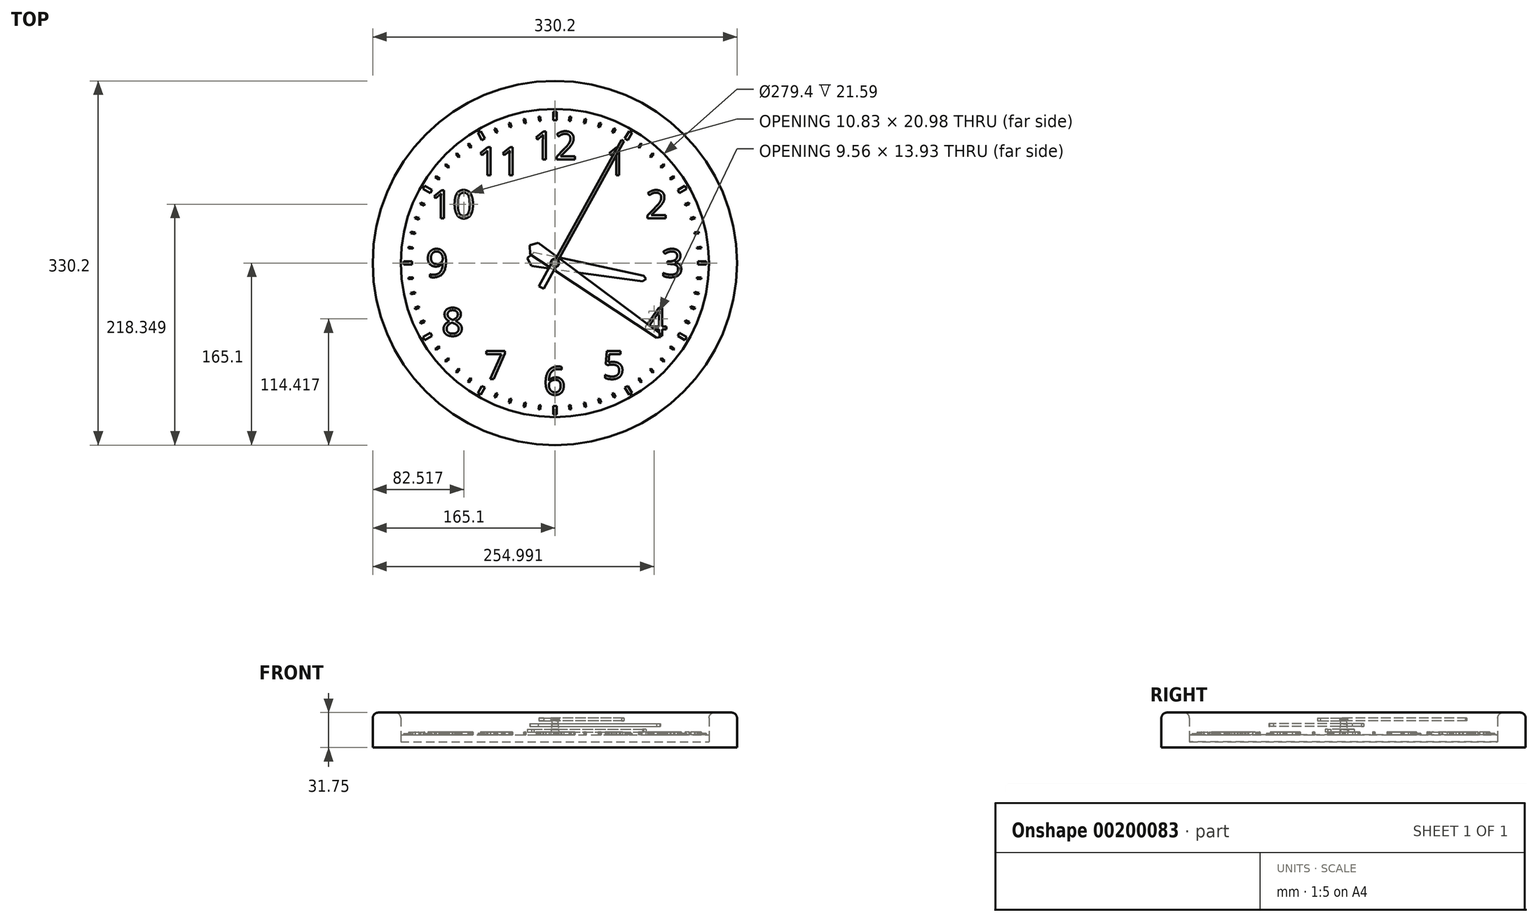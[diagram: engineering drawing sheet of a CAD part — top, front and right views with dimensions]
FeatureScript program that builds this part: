
annotation { "Feature Type Name" : "Feature", "Feature Type Description" : "" }
export const myFeature = defineFeature(function(context is Context, id is Id, definition is map)
    precondition{}
    {
        {
            var Q0;
            Q0=qCreatedBy(makeId("Front.planeOp"),FACE);
            var sketch = newSketch(context, id + "F0", { "sketchPlane" : qUnion([Q0])});
            skLineSegment(sketch, "E0", {"start": v(0, 0) * mm, "end": v(0, 54.8) * mm, "construction": true});
            skLineSegment(sketch, "E1.bottom", {"start": v(139.7, 0) * mm, "end": v(165.1, 0) * mm});
            skLineSegment(sketch, "E1.top", {"start": v(139.7, 31.75) * mm, "end": v(165.1, 31.75) * mm});
            skLineSegment(sketch, "E1.left", {"start": v(139.7, 5.08) * mm, "end": v(139.7, 31.75) * mm});
            skLineSegment(sketch, "E1.right", {"start": v(165.1, 0) * mm, "end": v(165.1, 31.75) * mm});
            skLineSegment(sketch, "E2", {"start": v(152.4, 0) * mm, "end": v(152.4, 31.75) * mm, "construction": true});
            skLineSegment(sketch, "E3.bottom", {"start": v(0, 0) * mm, "end": v(139.7, 0) * mm});
            skLineSegment(sketch, "E3.top", {"start": v(0, 5.08) * mm, "end": v(139.7, 5.08) * mm});
            skLineSegment(sketch, "E3.left", {"start": v(0, 0) * mm, "end": v(0, 5.08) * mm});
            skSolve(sketch);
        }
        {
            var Q0;
            Q0=makeQuery(id+"F0.imprint","IMPRINT",FACE,{"disambiguationData":[TD([[makeQuery(id+"F0.imprint","IMPRINT",EDGE,{"derivedFrom":sQuery(id+"F0.wireOp",EDGE,"E1.bottom")}),1.0]])]});
            var Q1;
            Q1=sQuery(id+"F0.wireOp",EDGE,"E0");
            revolve(context, id + "F1", {"entities" : qUnion([Q0]), "axis" : qUnion([Q1]), "revolveType" : RevolveType.FULL});
        }
        {
            var Q0;
            Q0=makeQuery(id+"F1.opRevolve","SWEPT_EDGE",EDGE,{"disambiguationData":[OSD([sQuery(id+"F0.wireOp",EDGE,"E1.top"),sQuery(id+"F0.wireOp",EDGE,"E1.left")])]});
            var Q1;
            Q1=makeQuery(id+"F1.opRevolve","SWEPT_EDGE",EDGE,{"disambiguationData":[OSD([sQuery(id+"F0.wireOp",EDGE,"E1.top"),sQuery(id+"F0.wireOp",EDGE,"E1.right")])]});
            fillet(context, id + "F2", {"entities" : qUnion([Q0, Q1]), "radius" : 5.08 * mm, "tangentPropagation" : true, "allowEdgeOverflow" : false});
        }
        {
            var Q0;
            Q0=makeQuery(id+"F1.opRevolve","SWEPT_FACE",FACE,{"disambiguationData":[OSD([sQuery(id+"F0.wireOp",EDGE,"E3.top")])]});
            extrude(context, id + "F3", {"entities" : qUnion([Q0]), "depth" : 6.35 * mm});
        }
        {
            var Q0;
            Q0=makeQuery(id+"F3.opExtrude","CAP_FACE",FACE,{"disambiguationData":[OSD([sQuery(id+"F0.wireOp",EDGE,"E3.top")])],"isStart":false});
            var sketch = newSketch(context, id + "F4", { "sketchPlane" : qUnion([Q0])});
            skText(sketch, "E4", { "text": "12", "fontName": "OpenSans-Regular.ttf"});
            skLineSegment(sketch, "E5", {"start": v(0, 0) * mm, "end": v(0, 106.68) * mm, "construction": true});
            skLineSegment(sketch, "E6.1.0", {"start": v(0, 0) * mm, "end": v(-53.34, 92.39) * mm, "construction": true});
            skLineSegment(sketch, "E6.2.0", {"start": v(0, 0) * mm, "end": v(-92.39, 53.34) * mm, "construction": true});
            skLineSegment(sketch, "E6.3.0", {"start": v(0, 0) * mm, "end": v(-106.68, 0) * mm, "construction": true});
            skLineSegment(sketch, "E6.4.0", {"start": v(0, 0) * mm, "end": v(-92.39, -53.34) * mm, "construction": true});
            skLineSegment(sketch, "E6.5.0", {"start": v(0, 0) * mm, "end": v(-53.34, -92.39) * mm, "construction": true});
            skLineSegment(sketch, "E6.6.0", {"start": v(0, 0) * mm, "end": v(0, -106.68) * mm, "construction": true});
            skLineSegment(sketch, "E6.7.0", {"start": v(0, 0) * mm, "end": v(53.34, -92.39) * mm, "construction": true});
            skLineSegment(sketch, "E6.8.0", {"start": v(0, 0) * mm, "end": v(92.39, -53.34) * mm, "construction": true});
            skLineSegment(sketch, "E6.9.0", {"start": v(0, 0) * mm, "end": v(106.68, 0) * mm, "construction": true});
            skLineSegment(sketch, "E6.10.0", {"start": v(0, 0) * mm, "end": v(92.39, 53.34) * mm, "construction": true});
            skLineSegment(sketch, "E6.11.0", {"start": v(0, 0) * mm, "end": v(53.34, 92.39) * mm, "construction": true});
            skPoint(sketch, "E6.center", {"position": v(0, 0) * mm});
            skText(sketch, "E7", { "text": "2", "fontName": "OpenSans-Regular.ttf"});
            skText(sketch, "E8", { "text": "3", "fontName": "OpenSans-Regular.ttf"});
            skText(sketch, "E9", { "text": "4", "fontName": "OpenSans-Regular.ttf"});
            skText(sketch, "E10", { "text": "1", "fontName": "OpenSans-Regular.ttf"});
            skText(sketch, "E11", { "text": "5", "fontName": "OpenSans-Regular.ttf"});
            skText(sketch, "E12", { "text": "6", "fontName": "OpenSans-Regular.ttf"});
            skText(sketch, "E13", { "text": "7", "fontName": "OpenSans-Regular.ttf"});
            skText(sketch, "E14", { "text": "9", "fontName": "OpenSans-Regular.ttf"});
            skText(sketch, "E15", { "text": "8", "fontName": "OpenSans-Regular.ttf"});
            skText(sketch, "E16", { "text": "10", "fontName": "OpenSans-Regular.ttf"});
            skText(sketch, "E17", { "text": "11", "fontName": "OpenSans-Regular.ttf"});
            const initialGuessF4  = {"E4": [-0.02037, 0.09398, 1, 0, 0.0254], "E7": [0.0821, 0.04064, 1, 0, 0.0254], "E8": [0.09649, -0.0127, 1, 0, 0.0254], "E9": [0.08151, -0.06604, 1, 0, 0.0254], "E10": [0.04604, 0.07969, 1, 0, 0.0254], "E11": [0.04313, -0.10509, 1, 0, 0.0254], "E12": [-0.01037, -0.11938, 1, 0, 0.0254], "E13": [-0.06367, -0.10509, 1, 0, 0.0254], "E14": [-0.11696, -0.0127, 1, 0, 0.0254], "E15": [-0.1027, -0.06604, 1, 0, 0.0254], "E16": [-0.11282, 0.04064, 1, 0, 0.0254], "E17": [-0.07073, 0.07969, 1, 0, 0.0254]};
            skSetInitialGuess(sketch, initialGuessF4);
            skSolve(sketch);
        }
        {
            var Q0;
            Q0=qSketchRegion(id+"F4",true);
            extrude(context, id + "F5", {"entities" : qUnion([Q0]), "depth" : 2.54 * mm});
        }
        {
            var Q0;
            Q0=makeQuery(id+"F3.opExtrude","CAP_FACE",FACE,{"disambiguationData":[OSD([sQuery(id+"F0.wireOp",EDGE,"E3.top")])],"isStart":false});
            var sketch = newSketch(context, id + "F6", { "sketchPlane" : qUnion([Q0])});
            skCircle(sketch, "E18", {"center": v(0, 0) * mm, "radius": 3.81 * mm});
            skSolve(sketch);
        }
        {
            var Q0;
            Q0=makeQuery(id+"F6.imprint","IMPRINT",FACE,{"disambiguationData":[TD([[makeQuery(id+"F6.imprint","IMPRINT",EDGE,{"derivedFrom":sQuery(id+"F6.wireOp",EDGE,"E18")}),-1.0]])]});
            cPlane(context, id + "F7", {"entities" : qUnion([Q0]), "cplaneType" : CPlaneType.OFFSET, "offset" : 13.97 * mm, "width" : 152.4 * mm, "height" : 152.4 * mm});
        }
        {
            var Q0;
            Q0=qCreatedBy(id+"F7.planeOp",FACE);
            var sketch = newSketch(context, id + "F8", { "sketchPlane" : qUnion([Q0])});
            skCircle(sketch, "E19", {"center": v(0, 0) * mm, "radius": 2.54 * mm});
            skSolve(sketch);
        }
        {
            var Q1;
            Q1=makeQuery(id+"F6.imprint","IMPRINT",FACE,{"disambiguationData":[TD([[makeQuery(id+"F6.imprint","IMPRINT",EDGE,{"derivedFrom":sQuery(id+"F6.wireOp",EDGE,"E18")}),1.0]])]});
            var Q2;
            Q2=makeQuery(id+"F8.imprint","IMPRINT",FACE,{"disambiguationData":[TD([[makeQuery(id+"F8.imprint","IMPRINT",EDGE,{"derivedFrom":sQuery(id+"F8.wireOp",EDGE,"E19")}),1.0]])]});
            loft(context, id + "F9", {"sheetProfilesArray" : [{ "sheetProfileEntities" : qUnion([Q1]) }, { "sheetProfileEntities" : qUnion([Q2]) }]});
        }
        {
            var Q0;
            Q0=makeQuery(id+"F3.opExtrude","CAP_FACE",FACE,{"disambiguationData":[OSD([sQuery(id+"F0.wireOp",EDGE,"E3.top")])],"isStart":false});
            cPlane(context, id + "F10", {"entities" : qUnion([Q0]), "cplaneType" : CPlaneType.OFFSET, "offset" : 2.54 * mm, "width" : 152.4 * mm, "height" : 152.4 * mm});
        }
        {
            var Q0;
            Q0=qCreatedBy(id+"F10.planeOp",FACE);
            var sketch = newSketch(context, id + "F11", { "sketchPlane" : qUnion([Q0])});
            skLineSegment(sketch, "E20", {"start": v(5, -0.88) * mm, "end": v(80.05, -14.11) * mm, "construction": true});
            skLineSegment(sketch, "E21", {"start": v(80.05, -14.11) * mm, "end": v(79.6, -16.62) * mm, "construction": true});
            skLineSegment(sketch, "E22", {"start": v(-20.01, 3.53) * mm, "end": v(-21.11, -2.72) * mm, "construction": true});
            skLineSegment(sketch, "E23", {"start": v(5, -0.88) * mm, "end": v(-25.01, 4.41) * mm, "construction": true});
            skLineSegment(sketch, "E24", {"start": v(-25.01, 4.41) * mm, "end": v(-21.11, -2.72) * mm});
            skLineSegment(sketch, "E25", {"start": v(-21.11, -2.72) * mm, "end": v(79.6, -16.62) * mm});
            skLineSegment(sketch, "E26", {"start": v(80.05, -14.11) * mm, "end": v(82.55, -14.56) * mm, "construction": true});
            skLineSegment(sketch, "E27", {"start": v(82.55, -14.56) * mm, "end": v(79.6, -16.62) * mm});
            skLineSegment(sketch, "E28.MirrorCS", {"start": v(82.55, -14.56) * mm, "end": v(80.49, -11.61) * mm});
            skLineSegment(sketch, "E29.MirrorCS", {"start": v(-18.9, 9.78) * mm, "end": v(80.49, -11.61) * mm});
            skLineSegment(sketch, "E30.MirrorCS", {"start": v(-25.01, 4.41) * mm, "end": v(-18.9, 9.78) * mm});
            skSolve(sketch);
        }
        {
            var Q0;
            Q0=makeQuery(id+"F11.imprint","IMPRINT",FACE,{"disambiguationData":[TD([[makeQuery(id+"F11.imprint","IMPRINT",EDGE,{"derivedFrom":sQuery(id+"F11.wireOp",EDGE,"E24")}),1.0]])]});
            var Q1;
            Q1=makeQuery(id+"F11.imprint","IMPRINT",FACE,{"disambiguationData":[TD([[makeQuery(id+"F11.imprint","IMPRINT",EDGE,{"derivedFrom":makeQuery(id+"F9.opLoft","MID_CAP_EDGE",EDGE,{"disambiguationData":[OSD([sQuery(id+"F6.wireOp",EDGE,"E18")])],"capPos":0.0})}),1.0]])]});
            extrude(context, id + "F12", {"entities" : qUnion([Q0, Q1]), "depth" : 2.54 * mm});
        }
        {
            var Q0;
            Q0=makeQuery(id+"F12.opExtrude","CAP_FACE",FACE,{"disambiguationData":[OSD([sQuery(id+"F11.wireOp",EDGE,"E24"),sQuery(id+"F11.wireOp",EDGE,"E25"),sQuery(id+"F11.wireOp",EDGE,"E27"),sQuery(id+"F11.wireOp",EDGE,"E28.MirrorCS"),sQuery(id+"F11.wireOp",EDGE,"E29.MirrorCS"),sQuery(id+"F11.wireOp",EDGE,"E30.MirrorCS")])],"isStart":false});
            cPlane(context, id + "F13", {"entities" : qUnion([Q0]), "cplaneType" : CPlaneType.OFFSET, "offset" : 2.54 * mm, "width" : 152.4 * mm, "height" : 152.4 * mm});
        }
        {
            var Q0;
            Q0=qCreatedBy(id+"F13.planeOp",FACE);
            var sketch = newSketch(context, id + "F14", { "sketchPlane" : qUnion([Q0])});
            skLineSegment(sketch, "E31", {"start": v(0, 0) * mm, "end": v(95.7, -67.02) * mm, "construction": true});
            skLineSegment(sketch, "E32", {"start": v(0, 0) * mm, "end": v(-22.89, 16.03) * mm, "construction": true});
            skLineSegment(sketch, "E33", {"start": v(-18.73, 13.11) * mm, "end": v(-15.08, 18.31) * mm, "construction": true});
            skLineSegment(sketch, "E34", {"start": v(93.63, -65.56) * mm, "end": v(95.09, -63.48) * mm, "construction": true});
            skLineSegment(sketch, "E35", {"start": v(-22.89, 16.03) * mm, "end": v(-15.08, 18.31) * mm});
            skLineSegment(sketch, "E36", {"start": v(-15.08, 18.31) * mm, "end": v(95.09, -63.48) * mm});
            skLineSegment(sketch, "E37", {"start": v(95.09, -63.48) * mm, "end": v(95.7, -67.02) * mm});
            skLineSegment(sketch, "E38.MirrorCS", {"start": v(-22.89, 16.03) * mm, "end": v(-22.37, 7.91) * mm});
            skLineSegment(sketch, "E39.MirrorCS", {"start": v(-22.37, 7.91) * mm, "end": v(92.17, -67.64) * mm});
            skLineSegment(sketch, "E40.MirrorCS", {"start": v(92.17, -67.64) * mm, "end": v(95.7, -67.02) * mm});
            skLineSegment(sketch, "E41", {"start": v(0, 0) * mm, "end": v(0, -35.35) * mm, "construction": true});
            skSolve(sketch);
        }
        {
            var Q0;
            Q0=makeQuery(id+"F14.imprint","IMPRINT",FACE,{"disambiguationData":[TD([[makeQuery(id+"F14.imprint","IMPRINT",EDGE,{"derivedFrom":sQuery(id+"F14.wireOp",EDGE,"E35")}),-1.0]])]});
            extrude(context, id + "F15", {"entities" : qUnion([Q0]), "depth" : 2.54 * mm});
        }
        {
            var Q0;
            Q0=makeQuery(id+"F15.opExtrude","CAP_FACE",FACE,{"disambiguationData":[OSD([sQuery(id+"F14.wireOp",EDGE,"E35"),sQuery(id+"F14.wireOp",EDGE,"E36"),sQuery(id+"F14.wireOp",EDGE,"E37"),sQuery(id+"F14.wireOp",EDGE,"E38.MirrorCS"),sQuery(id+"F14.wireOp",EDGE,"E39.MirrorCS"),sQuery(id+"F14.wireOp",EDGE,"E40.MirrorCS")])],"isStart":false});
            cPlane(context, id + "F16", {"entities" : qUnion([Q0]), "cplaneType" : CPlaneType.OFFSET, "offset" : 2.54 * mm, "width" : 152.4 * mm, "height" : 152.4 * mm});
        }
        {
            var Q0;
            Q0=qCreatedBy(id+"F16.planeOp",FACE);
            var sketch = newSketch(context, id + "F17", { "sketchPlane" : qUnion([Q0])});
            skArc(sketch, "E42", {"start": v(0.85, -3.72) * mm, "mid": v(3.63, -1.17) * mm, "end": v(2.85, 2.53) * mm});
            skLineSegment(sketch, "E43", {"start": v(0, 0) * mm, "end": v(61.55, 111.09) * mm, "construction": true});
            skLineSegment(sketch, "E44", {"start": v(0, 0) * mm, "end": v(-12.31, -22.22) * mm, "construction": true});
            skLineSegment(sketch, "E45", {"start": v(-12.31, -22.22) * mm, "end": v(-10.09, -23.45) * mm});
            skLineSegment(sketch, "E46", {"start": v(-10.09, -23.45) * mm, "end": v(0.85, -3.72) * mm});
            skLineSegment(sketch, "E47", {"start": v(61.55, 111.09) * mm, "end": v(62.66, 110.47) * mm});
            skLineSegment(sketch, "E48", {"start": v(62.66, 110.47) * mm, "end": v(2.85, 2.53) * mm});
            skLineSegment(sketch, "E49.MirrorCS", {"start": v(61.55, 111.09) * mm, "end": v(60.44, 111.7) * mm});
            skLineSegment(sketch, "E50.MirrorCS", {"start": v(60.44, 111.7) * mm, "end": v(0.63, 3.76) * mm});
            skArc(sketch, "E51.MirrorCS", {"start": v(-3.6, -1.25) * mm, "mid": v(-2.91, 2.46) * mm, "end": v(0.63, 3.76) * mm});
            skLineSegment(sketch, "E52.MirrorCS", {"start": v(-14.53, -20.99) * mm, "end": v(-3.6, -1.25) * mm});
            skLineSegment(sketch, "E53.MirrorCS", {"start": v(-12.31, -22.22) * mm, "end": v(-14.53, -20.99) * mm});
            skSolve(sketch);
        }
        {
            var Q0;
            Q0=makeQuery(id+"F17.imprint","IMPRINT",FACE,{"disambiguationData":[TD([[makeQuery(id+"F17.imprint","IMPRINT",EDGE,{"derivedFrom":sQuery(id+"F17.wireOp",EDGE,"E42")}),1.0]])]});
            extrude(context, id + "F18", {"entities" : qUnion([Q0]), "depth" : 2.54 * mm});
        }
        {
            var Q0;
            Q0=makeQuery(id+"F9.opLoft","SWEPT_BODY",BODY,{"disambiguationData":[OSD([makeQuery(id+"F6.imprint","IMPRINT",FACE,{"disambiguationData":[TD([[makeQuery(id+"F6.imprint","IMPRINT",EDGE,{"derivedFrom":sQuery(id+"F6.wireOp",EDGE,"E18")}),1.0]])]}),makeQuery(id+"F8.imprint","IMPRINT",FACE,{"disambiguationData":[TD([[makeQuery(id+"F8.imprint","IMPRINT",EDGE,{"derivedFrom":sQuery(id+"F8.wireOp",EDGE,"E19")}),1.0]])]})])]});
            var Q1;
            Q1=makeQuery(id+"F12.opExtrude","SWEPT_BODY",BODY,{"disambiguationData":[OSD([sQuery(id+"F11.wireOp",EDGE,"E24"),sQuery(id+"F11.wireOp",EDGE,"E25"),sQuery(id+"F11.wireOp",EDGE,"E27"),sQuery(id+"F11.wireOp",EDGE,"E28.MirrorCS"),sQuery(id+"F11.wireOp",EDGE,"E29.MirrorCS"),sQuery(id+"F11.wireOp",EDGE,"E30.MirrorCS")])]});
            booleanBodies(context, id + "F19", {"operationType" : BooleanOperationType.SUBTRACTION, "tools" : qUnion([Q0]), "targets" : qUnion([Q1]), "keepTools" : true});
        }
        {
            var Q0;
            Q0=makeQuery(id+"F9.opLoft","SWEPT_BODY",BODY,{"disambiguationData":[OSD([makeQuery(id+"F6.imprint","IMPRINT",FACE,{"disambiguationData":[TD([[makeQuery(id+"F6.imprint","IMPRINT",EDGE,{"derivedFrom":sQuery(id+"F6.wireOp",EDGE,"E18")}),1.0]])]}),makeQuery(id+"F8.imprint","IMPRINT",FACE,{"disambiguationData":[TD([[makeQuery(id+"F8.imprint","IMPRINT",EDGE,{"derivedFrom":sQuery(id+"F8.wireOp",EDGE,"E19")}),1.0]])]})])]});
            var Q1;
            Q1=makeQuery(id+"F15.opExtrude","SWEPT_BODY",BODY,{"disambiguationData":[OSD([sQuery(id+"F14.wireOp",EDGE,"E35"),sQuery(id+"F14.wireOp",EDGE,"E36"),sQuery(id+"F14.wireOp",EDGE,"E37"),sQuery(id+"F14.wireOp",EDGE,"E38.MirrorCS"),sQuery(id+"F14.wireOp",EDGE,"E39.MirrorCS"),sQuery(id+"F14.wireOp",EDGE,"E40.MirrorCS")])]});
            booleanBodies(context, id + "F20", {"operationType" : BooleanOperationType.SUBTRACTION, "tools" : qUnion([Q0]), "targets" : qUnion([Q1]), "keepTools" : true});
        }
        {
            var Q0;
            Q0=makeQuery(id+"F9.opLoft","SWEPT_BODY",BODY,{"disambiguationData":[OSD([makeQuery(id+"F6.imprint","IMPRINT",FACE,{"disambiguationData":[TD([[makeQuery(id+"F6.imprint","IMPRINT",EDGE,{"derivedFrom":sQuery(id+"F6.wireOp",EDGE,"E18")}),1.0]])]}),makeQuery(id+"F8.imprint","IMPRINT",FACE,{"disambiguationData":[TD([[makeQuery(id+"F8.imprint","IMPRINT",EDGE,{"derivedFrom":sQuery(id+"F8.wireOp",EDGE,"E19")}),1.0]])]})])]});
            var Q1;
            Q1=makeQuery(id+"F18.opExtrude","SWEPT_BODY",BODY,{"disambiguationData":[OSD([sQuery(id+"F17.wireOp",EDGE,"E42"),sQuery(id+"F17.wireOp",EDGE,"E45"),sQuery(id+"F17.wireOp",EDGE,"E46"),sQuery(id+"F17.wireOp",EDGE,"E47"),sQuery(id+"F17.wireOp",EDGE,"E48"),sQuery(id+"F17.wireOp",EDGE,"E49.MirrorCS"),sQuery(id+"F17.wireOp",EDGE,"E50.MirrorCS"),sQuery(id+"F17.wireOp",EDGE,"E51.MirrorCS"),sQuery(id+"F17.wireOp",EDGE,"E52.MirrorCS"),sQuery(id+"F17.wireOp",EDGE,"E53.MirrorCS")])]});
            booleanBodies(context, id + "F21", {"operationType" : BooleanOperationType.SUBTRACTION, "tools" : qUnion([Q0]), "targets" : qUnion([Q1]), "keepTools" : true});
        }
        {
            var Q0;
            Q0=makeQuery(id+"F19.opBoolean","INTERSECT",EDGE,{"derivedFrom":[makeQuery(id+"F9.opLoft","SWEPT_FACE",FACE,{"disambiguationData":[OSD([sQuery(id+"F6.wireOp",EDGE,"E18"),sQuery(id+"F8.wireOp",EDGE,"E19")])]}),makeQuery(id+"F12.opExtrude","CAP_FACE",FACE,{"disambiguationData":[OSD([sQuery(id+"F11.wireOp",EDGE,"E24"),sQuery(id+"F11.wireOp",EDGE,"E25"),sQuery(id+"F11.wireOp",EDGE,"E27"),sQuery(id+"F11.wireOp",EDGE,"E28.MirrorCS"),sQuery(id+"F11.wireOp",EDGE,"E29.MirrorCS"),sQuery(id+"F11.wireOp",EDGE,"E30.MirrorCS")])],"isStart":true})]});
            var Q1;
            Q1=makeQuery(id+"F19.opBoolean","INTERSECT",EDGE,{"derivedFrom":[makeQuery(id+"F9.opLoft","SWEPT_FACE",FACE,{"disambiguationData":[OSD([sQuery(id+"F6.wireOp",EDGE,"E18"),sQuery(id+"F8.wireOp",EDGE,"E19")])]}),makeQuery(id+"F12.opExtrude","CAP_FACE",FACE,{"disambiguationData":[OSD([sQuery(id+"F11.wireOp",EDGE,"E24"),sQuery(id+"F11.wireOp",EDGE,"E25"),sQuery(id+"F11.wireOp",EDGE,"E27"),sQuery(id+"F11.wireOp",EDGE,"E28.MirrorCS"),sQuery(id+"F11.wireOp",EDGE,"E29.MirrorCS"),sQuery(id+"F11.wireOp",EDGE,"E30.MirrorCS")])],"isStart":false})]});
            var Q2;
            Q2=makeQuery(id+"F20.opBoolean","INTERSECT",EDGE,{"derivedFrom":[makeQuery(id+"F9.opLoft","SWEPT_FACE",FACE,{"disambiguationData":[OSD([sQuery(id+"F6.wireOp",EDGE,"E18"),sQuery(id+"F8.wireOp",EDGE,"E19")])]}),makeQuery(id+"F15.opExtrude","CAP_FACE",FACE,{"disambiguationData":[OSD([sQuery(id+"F14.wireOp",EDGE,"E35"),sQuery(id+"F14.wireOp",EDGE,"E36"),sQuery(id+"F14.wireOp",EDGE,"E37"),sQuery(id+"F14.wireOp",EDGE,"E38.MirrorCS"),sQuery(id+"F14.wireOp",EDGE,"E39.MirrorCS"),sQuery(id+"F14.wireOp",EDGE,"E40.MirrorCS")])],"isStart":true})]});
            var Q3;
            Q3=makeQuery(id+"F20.opBoolean","INTERSECT",EDGE,{"derivedFrom":[makeQuery(id+"F9.opLoft","SWEPT_FACE",FACE,{"disambiguationData":[OSD([sQuery(id+"F6.wireOp",EDGE,"E18"),sQuery(id+"F8.wireOp",EDGE,"E19")])]}),makeQuery(id+"F15.opExtrude","CAP_FACE",FACE,{"disambiguationData":[OSD([sQuery(id+"F14.wireOp",EDGE,"E35"),sQuery(id+"F14.wireOp",EDGE,"E36"),sQuery(id+"F14.wireOp",EDGE,"E37"),sQuery(id+"F14.wireOp",EDGE,"E38.MirrorCS"),sQuery(id+"F14.wireOp",EDGE,"E39.MirrorCS"),sQuery(id+"F14.wireOp",EDGE,"E40.MirrorCS")])],"isStart":false})]});
            var Q4;
            Q4=makeQuery(id+"F21.opBoolean","INTERSECT",EDGE,{"derivedFrom":[makeQuery(id+"F9.opLoft","SWEPT_FACE",FACE,{"disambiguationData":[OSD([sQuery(id+"F6.wireOp",EDGE,"E18"),sQuery(id+"F8.wireOp",EDGE,"E19")])]}),makeQuery(id+"F18.opExtrude","CAP_FACE",FACE,{"disambiguationData":[OSD([sQuery(id+"F17.wireOp",EDGE,"E42"),sQuery(id+"F17.wireOp",EDGE,"E45"),sQuery(id+"F17.wireOp",EDGE,"E46"),sQuery(id+"F17.wireOp",EDGE,"E47"),sQuery(id+"F17.wireOp",EDGE,"E48"),sQuery(id+"F17.wireOp",EDGE,"E49.MirrorCS"),sQuery(id+"F17.wireOp",EDGE,"E50.MirrorCS"),sQuery(id+"F17.wireOp",EDGE,"E51.MirrorCS"),sQuery(id+"F17.wireOp",EDGE,"E52.MirrorCS"),sQuery(id+"F17.wireOp",EDGE,"E53.MirrorCS")])],"isStart":true})]});
            var Q5;
            Q5=makeQuery(id+"F21.opBoolean","COPY",EDGE,{"derivedFrom":makeQuery(id+"F9.opLoft","MID_CAP_EDGE",EDGE,{"disambiguationData":[OSD([sQuery(id+"F6.wireOp",EDGE,"E18"),sQuery(id+"F8.wireOp",EDGE,"E19")])],"capPos":1.0})});
            chamfer(context, id + "F22", {"entities" : qUnion([Q0, Q1, Q2, Q3, Q4, Q5]), "width" : 0.25 * mm, "tangentPropagation" : true});
        }
        {
            var Q0;
            Q0=makeQuery(id+"F3.opExtrude","CAP_FACE",FACE,{"disambiguationData":[OSD([sQuery(id+"F0.wireOp",EDGE,"E3.top")])],"isStart":false});
            var sketch = newSketch(context, id + "F23", { "sketchPlane" : qUnion([Q0])});
            skLineSegment(sketch, "E54", {"start": v(0, 0) * mm, "end": v(0, 139.7) * mm, "construction": true});
            skLineSegment(sketch, "E55.bottom", {"start": v(1.52, 137.16) * mm, "end": v(-1.52, 137.16) * mm});
            skLineSegment(sketch, "E55.top", {"start": v(1.52, 129.54) * mm, "end": v(-1.52, 129.54) * mm});
            skLineSegment(sketch, "E55.left", {"start": v(1.52, 137.16) * mm, "end": v(1.52, 129.54) * mm});
            skLineSegment(sketch, "E55.right", {"start": v(-1.52, 137.16) * mm, "end": v(-1.52, 129.54) * mm});
            skPoint(sketch, "E55.middle", {"position": v(0, 133.35) * mm});
            skSolve(sketch);
        }
        {
            var Q0;
            Q0=makeQuery(id+"F23.imprint","IMPRINT",FACE,{"disambiguationData":[TD([[makeQuery(id+"F23.imprint","IMPRINT",EDGE,{"derivedFrom":sQuery(id+"F23.wireOp",EDGE,"E55.bottom")}),1.0]])]});
            extrude(context, id + "F24", {"entities" : qUnion([Q0]), "depth" : 1.27 * mm});
        }
        {
            var Q0;
            Q0=makeQuery(id+"F24.opExtrude","SWEPT_BODY",BODY,{"disambiguationData":[OSD([sQuery(id+"F23.wireOp",EDGE,"E55.bottom"),sQuery(id+"F23.wireOp",EDGE,"E55.top"),sQuery(id+"F23.wireOp",EDGE,"E55.left"),sQuery(id+"F23.wireOp",EDGE,"E55.right")])]});
            var Q1;
            Q1=sQuery(id+"F0.wireOp",EDGE,"E0");
            circularPattern(context, id + "F25", {"entities" : qUnion([Q0]), "axis" : qUnion([Q1]), "angle" : 360 * degree, "instanceCount" : 12, "equalSpace" : true});
        }
        {
            var Q0;
            Q0=makeQuery(id+"F3.opExtrude","CAP_FACE",FACE,{"disambiguationData":[OSD([sQuery(id+"F0.wireOp",EDGE,"E3.top")])],"isStart":false});
            var sketch = newSketch(context, id + "F26", { "sketchPlane" : qUnion([Q0])});
            skLineSegment(sketch, "E56", {"start": v(0, 0) * mm, "end": v(0, 65.46) * mm, "construction": true});
            skLineSegment(sketch, "E57", {"start": v(0, 0) * mm, "end": v(13.94, 132.62) * mm, "construction": true});
            skLineSegment(sketch, "E58", {"start": v(13.54, 128.83) * mm, "end": v(14.3, 128.75) * mm});
            skLineSegment(sketch, "E59", {"start": v(13.94, 132.62) * mm, "end": v(14.7, 132.54) * mm});
            skLineSegment(sketch, "E60", {"start": v(14.7, 132.54) * mm, "end": v(14.3, 128.75) * mm});
            skLineSegment(sketch, "E61.MirrorCS", {"start": v(13.94, 132.62) * mm, "end": v(13.18, 132.7) * mm});
            skLineSegment(sketch, "E62.MirrorCS", {"start": v(13.18, 132.7) * mm, "end": v(12.78, 128.91) * mm});
            skLineSegment(sketch, "E63.MirrorCS", {"start": v(13.54, 128.83) * mm, "end": v(12.78, 128.91) * mm});
            skLineSegment(sketch, "E64.2.0", {"start": v(-13.18, 132.7) * mm, "end": v(-12.78, 128.91) * mm});
            skLineSegment(sketch, "E64.2.1", {"start": v(-13.94, 132.62) * mm, "end": v(-13.18, 132.7) * mm});
            skLineSegment(sketch, "E64.2.2", {"start": v(-13.94, 132.62) * mm, "end": v(-14.7, 132.54) * mm});
            skLineSegment(sketch, "E64.2.3", {"start": v(-14.7, 132.54) * mm, "end": v(-14.3, 128.75) * mm});
            skLineSegment(sketch, "E64.2.4", {"start": v(-13.54, 128.83) * mm, "end": v(-14.3, 128.75) * mm});
            skLineSegment(sketch, "E64.2.5", {"start": v(-13.54, 128.83) * mm, "end": v(-12.78, 128.91) * mm});
            skLineSegment(sketch, "E64.3.0", {"start": v(-26.98, 130.6) * mm, "end": v(-26.19, 126.87) * mm});
            skLineSegment(sketch, "E64.3.1", {"start": v(-27.73, 130.44) * mm, "end": v(-26.98, 130.6) * mm});
            skLineSegment(sketch, "E64.3.2", {"start": v(-27.73, 130.44) * mm, "end": v(-28.47, 130.28) * mm});
            skLineSegment(sketch, "E64.3.3", {"start": v(-28.47, 130.28) * mm, "end": v(-27.68, 126.55) * mm});
            skLineSegment(sketch, "E64.3.4", {"start": v(-26.93, 126.7) * mm, "end": v(-27.68, 126.55) * mm});
            skLineSegment(sketch, "E64.3.5", {"start": v(-26.93, 126.7) * mm, "end": v(-26.19, 126.87) * mm});
            skLineSegment(sketch, "E64.4.0", {"start": v(-40.48, 127.06) * mm, "end": v(-39.3, 123.44) * mm});
            skLineSegment(sketch, "E64.4.1", {"start": v(-41.2, 126.82) * mm, "end": v(-40.48, 127.06) * mm});
            skLineSegment(sketch, "E64.4.2", {"start": v(-41.2, 126.82) * mm, "end": v(-41.93, 126.59) * mm});
            skLineSegment(sketch, "E64.4.3", {"start": v(-41.93, 126.59) * mm, "end": v(-40.75, 122.96) * mm});
            skLineSegment(sketch, "E64.4.4", {"start": v(-40.03, 123.2) * mm, "end": v(-40.75, 122.96) * mm});
            skLineSegment(sketch, "E64.4.5", {"start": v(-40.03, 123.2) * mm, "end": v(-39.3, 123.44) * mm});
            skLineSegment(sketch, "E64.5.0", {"start": v(-53.54, 122.13) * mm, "end": v(-52, 118.65) * mm});
            skLineSegment(sketch, "E64.5.1", {"start": v(-54.24, 121.82) * mm, "end": v(-53.54, 122.13) * mm});
            skLineSegment(sketch, "E64.5.2", {"start": v(-54.24, 121.82) * mm, "end": v(-54.93, 121.51) * mm});
            skLineSegment(sketch, "E64.5.3", {"start": v(-54.93, 121.51) * mm, "end": v(-53.38, 118.03) * mm});
            skLineSegment(sketch, "E64.5.4", {"start": v(-52.69, 118.34) * mm, "end": v(-53.38, 118.03) * mm});
            skLineSegment(sketch, "E64.5.5", {"start": v(-52.69, 118.34) * mm, "end": v(-52, 118.65) * mm});
            skLineSegment(sketch, "E64.7.0", {"start": v(-77.76, 108.33) * mm, "end": v(-75.53, 105.25) * mm});
            skLineSegment(sketch, "E64.7.1", {"start": v(-78.38, 107.88) * mm, "end": v(-77.76, 108.33) * mm});
            skLineSegment(sketch, "E64.7.2", {"start": v(-78.38, 107.88) * mm, "end": v(-79, 107.43) * mm});
            skLineSegment(sketch, "E64.7.3", {"start": v(-79, 107.43) * mm, "end": v(-76.76, 104.35) * mm});
            skLineSegment(sketch, "E64.7.4", {"start": v(-76.14, 104.8) * mm, "end": v(-76.76, 104.35) * mm});
            skLineSegment(sketch, "E64.7.5", {"start": v(-76.14, 104.8) * mm, "end": v(-75.53, 105.25) * mm});
            skLineSegment(sketch, "E64.8.0", {"start": v(-88.66, 99.6) * mm, "end": v(-86.11, 96.78) * mm});
            skLineSegment(sketch, "E64.8.1", {"start": v(-89.23, 99.1) * mm, "end": v(-88.66, 99.6) * mm});
            skLineSegment(sketch, "E64.8.2", {"start": v(-89.23, 99.1) * mm, "end": v(-89.8, 98.59) * mm});
            skLineSegment(sketch, "E64.8.3", {"start": v(-89.8, 98.59) * mm, "end": v(-87.25, 95.76) * mm});
            skLineSegment(sketch, "E64.8.4", {"start": v(-86.68, 96.27) * mm, "end": v(-87.25, 95.76) * mm});
            skLineSegment(sketch, "E64.8.5", {"start": v(-86.68, 96.27) * mm, "end": v(-86.11, 96.78) * mm});
            skLineSegment(sketch, "E64.9.0", {"start": v(-98.59, 89.8) * mm, "end": v(-95.76, 87.25) * mm});
            skLineSegment(sketch, "E64.9.1", {"start": v(-99.1, 89.23) * mm, "end": v(-98.59, 89.8) * mm});
            skLineSegment(sketch, "E64.9.2", {"start": v(-99.1, 89.23) * mm, "end": v(-99.6, 88.66) * mm});
            skLineSegment(sketch, "E64.9.3", {"start": v(-99.6, 88.66) * mm, "end": v(-96.78, 86.11) * mm});
            skLineSegment(sketch, "E64.9.4", {"start": v(-96.27, 86.68) * mm, "end": v(-96.78, 86.11) * mm});
            skLineSegment(sketch, "E64.9.5", {"start": v(-96.27, 86.68) * mm, "end": v(-95.76, 87.25) * mm});
            skLineSegment(sketch, "E64.10.0", {"start": v(-107.43, 79) * mm, "end": v(-104.35, 76.76) * mm});
            skLineSegment(sketch, "E64.10.1", {"start": v(-107.88, 78.38) * mm, "end": v(-107.43, 79) * mm});
            skLineSegment(sketch, "E64.10.2", {"start": v(-107.88, 78.38) * mm, "end": v(-108.33, 77.76) * mm});
            skLineSegment(sketch, "E64.10.3", {"start": v(-108.33, 77.76) * mm, "end": v(-105.25, 75.53) * mm});
            skLineSegment(sketch, "E64.10.4", {"start": v(-104.8, 76.14) * mm, "end": v(-105.25, 75.53) * mm});
            skLineSegment(sketch, "E64.10.5", {"start": v(-104.8, 76.14) * mm, "end": v(-104.35, 76.76) * mm});
            skLineSegment(sketch, "E64.12.0", {"start": v(-121.51, 54.93) * mm, "end": v(-118.03, 53.38) * mm});
            skLineSegment(sketch, "E64.12.1", {"start": v(-121.82, 54.24) * mm, "end": v(-121.51, 54.93) * mm});
            skLineSegment(sketch, "E64.12.2", {"start": v(-121.82, 54.24) * mm, "end": v(-122.13, 53.54) * mm});
            skLineSegment(sketch, "E64.12.3", {"start": v(-122.13, 53.54) * mm, "end": v(-118.65, 52) * mm});
            skLineSegment(sketch, "E64.12.4", {"start": v(-118.34, 52.69) * mm, "end": v(-118.65, 52) * mm});
            skLineSegment(sketch, "E64.12.5", {"start": v(-118.34, 52.69) * mm, "end": v(-118.03, 53.38) * mm});
            skLineSegment(sketch, "E64.13.0", {"start": v(-126.59, 41.93) * mm, "end": v(-122.96, 40.75) * mm});
            skLineSegment(sketch, "E64.13.1", {"start": v(-126.82, 41.2) * mm, "end": v(-126.59, 41.93) * mm});
            skLineSegment(sketch, "E64.13.2", {"start": v(-126.82, 41.2) * mm, "end": v(-127.06, 40.48) * mm});
            skLineSegment(sketch, "E64.13.3", {"start": v(-127.06, 40.48) * mm, "end": v(-123.44, 39.3) * mm});
            skLineSegment(sketch, "E64.13.4", {"start": v(-123.2, 40.03) * mm, "end": v(-123.44, 39.3) * mm});
            skLineSegment(sketch, "E64.13.5", {"start": v(-123.2, 40.03) * mm, "end": v(-122.96, 40.75) * mm});
            skLineSegment(sketch, "E64.14.0", {"start": v(-130.28, 28.47) * mm, "end": v(-126.55, 27.68) * mm});
            skLineSegment(sketch, "E64.14.1", {"start": v(-130.44, 27.73) * mm, "end": v(-130.28, 28.47) * mm});
            skLineSegment(sketch, "E64.14.2", {"start": v(-130.44, 27.73) * mm, "end": v(-130.6, 26.98) * mm});
            skLineSegment(sketch, "E64.14.3", {"start": v(-130.6, 26.98) * mm, "end": v(-126.87, 26.19) * mm});
            skLineSegment(sketch, "E64.14.4", {"start": v(-126.7, 26.93) * mm, "end": v(-126.87, 26.19) * mm});
            skLineSegment(sketch, "E64.14.5", {"start": v(-126.7, 26.93) * mm, "end": v(-126.55, 27.68) * mm});
            skLineSegment(sketch, "E64.15.0", {"start": v(-132.54, 14.7) * mm, "end": v(-128.75, 14.3) * mm});
            skLineSegment(sketch, "E64.15.1", {"start": v(-132.62, 13.94) * mm, "end": v(-132.54, 14.7) * mm});
            skLineSegment(sketch, "E64.15.2", {"start": v(-132.62, 13.94) * mm, "end": v(-132.7, 13.18) * mm});
            skLineSegment(sketch, "E64.15.3", {"start": v(-132.7, 13.18) * mm, "end": v(-128.91, 12.78) * mm});
            skLineSegment(sketch, "E64.15.4", {"start": v(-128.83, 13.54) * mm, "end": v(-128.91, 12.78) * mm});
            skLineSegment(sketch, "E64.15.5", {"start": v(-128.83, 13.54) * mm, "end": v(-128.75, 14.3) * mm});
            skLineSegment(sketch, "E64.17.0", {"start": v(-132.7, -13.18) * mm, "end": v(-128.91, -12.78) * mm});
            skLineSegment(sketch, "E64.17.1", {"start": v(-132.62, -13.94) * mm, "end": v(-132.7, -13.18) * mm});
            skLineSegment(sketch, "E64.17.2", {"start": v(-132.62, -13.94) * mm, "end": v(-132.54, -14.7) * mm});
            skLineSegment(sketch, "E64.17.3", {"start": v(-132.54, -14.7) * mm, "end": v(-128.75, -14.3) * mm});
            skLineSegment(sketch, "E64.17.4", {"start": v(-128.83, -13.54) * mm, "end": v(-128.75, -14.3) * mm});
            skLineSegment(sketch, "E64.17.5", {"start": v(-128.83, -13.54) * mm, "end": v(-128.91, -12.78) * mm});
            skLineSegment(sketch, "E64.18.0", {"start": v(-130.6, -26.98) * mm, "end": v(-126.87, -26.19) * mm});
            skLineSegment(sketch, "E64.18.1", {"start": v(-130.44, -27.73) * mm, "end": v(-130.6, -26.98) * mm});
            skLineSegment(sketch, "E64.18.2", {"start": v(-130.44, -27.73) * mm, "end": v(-130.28, -28.47) * mm});
            skLineSegment(sketch, "E64.18.3", {"start": v(-130.28, -28.47) * mm, "end": v(-126.55, -27.68) * mm});
            skLineSegment(sketch, "E64.18.4", {"start": v(-126.7, -26.93) * mm, "end": v(-126.55, -27.68) * mm});
            skLineSegment(sketch, "E64.18.5", {"start": v(-126.7, -26.93) * mm, "end": v(-126.87, -26.19) * mm});
            skLineSegment(sketch, "E64.19.0", {"start": v(-127.06, -40.48) * mm, "end": v(-123.44, -39.3) * mm});
            skLineSegment(sketch, "E64.19.1", {"start": v(-126.82, -41.2) * mm, "end": v(-127.06, -40.48) * mm});
            skLineSegment(sketch, "E64.19.2", {"start": v(-126.82, -41.2) * mm, "end": v(-126.59, -41.93) * mm});
            skLineSegment(sketch, "E64.19.3", {"start": v(-126.59, -41.93) * mm, "end": v(-122.96, -40.75) * mm});
            skLineSegment(sketch, "E64.19.4", {"start": v(-123.2, -40.03) * mm, "end": v(-122.96, -40.75) * mm});
            skLineSegment(sketch, "E64.19.5", {"start": v(-123.2, -40.03) * mm, "end": v(-123.44, -39.3) * mm});
            skLineSegment(sketch, "E64.20.0", {"start": v(-122.13, -53.54) * mm, "end": v(-118.65, -52) * mm});
            skLineSegment(sketch, "E64.20.1", {"start": v(-121.82, -54.24) * mm, "end": v(-122.13, -53.54) * mm});
            skLineSegment(sketch, "E64.20.2", {"start": v(-121.82, -54.24) * mm, "end": v(-121.51, -54.93) * mm});
            skLineSegment(sketch, "E64.20.3", {"start": v(-121.51, -54.93) * mm, "end": v(-118.03, -53.38) * mm});
            skLineSegment(sketch, "E64.20.4", {"start": v(-118.34, -52.69) * mm, "end": v(-118.03, -53.38) * mm});
            skLineSegment(sketch, "E64.20.5", {"start": v(-118.34, -52.69) * mm, "end": v(-118.65, -52) * mm});
            skLineSegment(sketch, "E64.22.0", {"start": v(-108.33, -77.76) * mm, "end": v(-105.25, -75.53) * mm});
            skLineSegment(sketch, "E64.22.1", {"start": v(-107.88, -78.38) * mm, "end": v(-108.33, -77.76) * mm});
            skLineSegment(sketch, "E64.22.2", {"start": v(-107.88, -78.38) * mm, "end": v(-107.43, -79) * mm});
            skLineSegment(sketch, "E64.22.3", {"start": v(-107.43, -79) * mm, "end": v(-104.35, -76.76) * mm});
            skLineSegment(sketch, "E64.22.4", {"start": v(-104.8, -76.14) * mm, "end": v(-104.35, -76.76) * mm});
            skLineSegment(sketch, "E64.22.5", {"start": v(-104.8, -76.14) * mm, "end": v(-105.25, -75.53) * mm});
            skLineSegment(sketch, "E64.23.0", {"start": v(-99.6, -88.66) * mm, "end": v(-96.78, -86.11) * mm});
            skLineSegment(sketch, "E64.23.1", {"start": v(-99.1, -89.23) * mm, "end": v(-99.6, -88.66) * mm});
            skLineSegment(sketch, "E64.23.2", {"start": v(-99.1, -89.23) * mm, "end": v(-98.59, -89.8) * mm});
            skLineSegment(sketch, "E64.23.3", {"start": v(-98.59, -89.8) * mm, "end": v(-95.76, -87.25) * mm});
            skLineSegment(sketch, "E64.23.4", {"start": v(-96.27, -86.68) * mm, "end": v(-95.76, -87.25) * mm});
            skLineSegment(sketch, "E64.23.5", {"start": v(-96.27, -86.68) * mm, "end": v(-96.78, -86.11) * mm});
            skLineSegment(sketch, "E64.24.0", {"start": v(-89.8, -98.59) * mm, "end": v(-87.25, -95.76) * mm});
            skLineSegment(sketch, "E64.24.1", {"start": v(-89.23, -99.1) * mm, "end": v(-89.8, -98.59) * mm});
            skLineSegment(sketch, "E64.24.2", {"start": v(-89.23, -99.1) * mm, "end": v(-88.66, -99.6) * mm});
            skLineSegment(sketch, "E64.24.3", {"start": v(-88.66, -99.6) * mm, "end": v(-86.11, -96.78) * mm});
            skLineSegment(sketch, "E64.24.4", {"start": v(-86.68, -96.27) * mm, "end": v(-86.11, -96.78) * mm});
            skLineSegment(sketch, "E64.24.5", {"start": v(-86.68, -96.27) * mm, "end": v(-87.25, -95.76) * mm});
            skLineSegment(sketch, "E64.25.0", {"start": v(-79, -107.43) * mm, "end": v(-76.76, -104.35) * mm});
            skLineSegment(sketch, "E64.25.1", {"start": v(-78.38, -107.88) * mm, "end": v(-79, -107.43) * mm});
            skLineSegment(sketch, "E64.25.2", {"start": v(-78.38, -107.88) * mm, "end": v(-77.76, -108.33) * mm});
            skLineSegment(sketch, "E64.25.3", {"start": v(-77.76, -108.33) * mm, "end": v(-75.53, -105.25) * mm});
            skLineSegment(sketch, "E64.25.4", {"start": v(-76.14, -104.8) * mm, "end": v(-75.53, -105.25) * mm});
            skLineSegment(sketch, "E64.25.5", {"start": v(-76.14, -104.8) * mm, "end": v(-76.76, -104.35) * mm});
            skLineSegment(sketch, "E64.27.0", {"start": v(-54.93, -121.51) * mm, "end": v(-53.38, -118.03) * mm});
            skLineSegment(sketch, "E64.27.1", {"start": v(-54.24, -121.82) * mm, "end": v(-54.93, -121.51) * mm});
            skLineSegment(sketch, "E64.27.2", {"start": v(-54.24, -121.82) * mm, "end": v(-53.54, -122.13) * mm});
            skLineSegment(sketch, "E64.27.3", {"start": v(-53.54, -122.13) * mm, "end": v(-52, -118.65) * mm});
            skLineSegment(sketch, "E64.27.4", {"start": v(-52.69, -118.34) * mm, "end": v(-52, -118.65) * mm});
            skLineSegment(sketch, "E64.27.5", {"start": v(-52.69, -118.34) * mm, "end": v(-53.38, -118.03) * mm});
            skLineSegment(sketch, "E64.28.0", {"start": v(-41.93, -126.59) * mm, "end": v(-40.75, -122.96) * mm});
            skLineSegment(sketch, "E64.28.1", {"start": v(-41.2, -126.82) * mm, "end": v(-41.93, -126.59) * mm});
            skLineSegment(sketch, "E64.28.2", {"start": v(-41.2, -126.82) * mm, "end": v(-40.48, -127.06) * mm});
            skLineSegment(sketch, "E64.28.3", {"start": v(-40.48, -127.06) * mm, "end": v(-39.3, -123.44) * mm});
            skLineSegment(sketch, "E64.28.4", {"start": v(-40.03, -123.2) * mm, "end": v(-39.3, -123.44) * mm});
            skLineSegment(sketch, "E64.28.5", {"start": v(-40.03, -123.2) * mm, "end": v(-40.75, -122.96) * mm});
            skLineSegment(sketch, "E64.29.0", {"start": v(-28.47, -130.28) * mm, "end": v(-27.68, -126.55) * mm});
            skLineSegment(sketch, "E64.29.1", {"start": v(-27.73, -130.44) * mm, "end": v(-28.47, -130.28) * mm});
            skLineSegment(sketch, "E64.29.2", {"start": v(-27.73, -130.44) * mm, "end": v(-26.98, -130.6) * mm});
            skLineSegment(sketch, "E64.29.3", {"start": v(-26.98, -130.6) * mm, "end": v(-26.19, -126.87) * mm});
            skLineSegment(sketch, "E64.29.4", {"start": v(-26.93, -126.7) * mm, "end": v(-26.19, -126.87) * mm});
            skLineSegment(sketch, "E64.29.5", {"start": v(-26.93, -126.7) * mm, "end": v(-27.68, -126.55) * mm});
            skLineSegment(sketch, "E64.30.0", {"start": v(-14.7, -132.54) * mm, "end": v(-14.3, -128.75) * mm});
            skLineSegment(sketch, "E64.30.1", {"start": v(-13.94, -132.62) * mm, "end": v(-14.7, -132.54) * mm});
            skLineSegment(sketch, "E64.30.2", {"start": v(-13.94, -132.62) * mm, "end": v(-13.18, -132.7) * mm});
            skLineSegment(sketch, "E64.30.3", {"start": v(-13.18, -132.7) * mm, "end": v(-12.78, -128.91) * mm});
            skLineSegment(sketch, "E64.30.4", {"start": v(-13.54, -128.83) * mm, "end": v(-12.78, -128.91) * mm});
            skLineSegment(sketch, "E64.30.5", {"start": v(-13.54, -128.83) * mm, "end": v(-14.3, -128.75) * mm});
            skLineSegment(sketch, "E64.32.0", {"start": v(13.18, -132.7) * mm, "end": v(12.78, -128.91) * mm});
            skLineSegment(sketch, "E64.32.1", {"start": v(13.94, -132.62) * mm, "end": v(13.18, -132.7) * mm});
            skLineSegment(sketch, "E64.32.2", {"start": v(13.94, -132.62) * mm, "end": v(14.7, -132.54) * mm});
            skLineSegment(sketch, "E64.32.3", {"start": v(14.7, -132.54) * mm, "end": v(14.3, -128.75) * mm});
            skLineSegment(sketch, "E64.32.4", {"start": v(13.54, -128.83) * mm, "end": v(14.3, -128.75) * mm});
            skLineSegment(sketch, "E64.32.5", {"start": v(13.54, -128.83) * mm, "end": v(12.78, -128.91) * mm});
            skLineSegment(sketch, "E64.33.0", {"start": v(26.98, -130.6) * mm, "end": v(26.19, -126.87) * mm});
            skLineSegment(sketch, "E64.33.1", {"start": v(27.73, -130.44) * mm, "end": v(26.98, -130.6) * mm});
            skLineSegment(sketch, "E64.33.2", {"start": v(27.73, -130.44) * mm, "end": v(28.47, -130.28) * mm});
            skLineSegment(sketch, "E64.33.3", {"start": v(28.47, -130.28) * mm, "end": v(27.68, -126.55) * mm});
            skLineSegment(sketch, "E64.33.4", {"start": v(26.93, -126.7) * mm, "end": v(27.68, -126.55) * mm});
            skLineSegment(sketch, "E64.33.5", {"start": v(26.93, -126.7) * mm, "end": v(26.19, -126.87) * mm});
            skLineSegment(sketch, "E64.34.0", {"start": v(40.48, -127.06) * mm, "end": v(39.3, -123.44) * mm});
            skLineSegment(sketch, "E64.34.1", {"start": v(41.2, -126.82) * mm, "end": v(40.48, -127.06) * mm});
            skLineSegment(sketch, "E64.34.2", {"start": v(41.2, -126.82) * mm, "end": v(41.93, -126.59) * mm});
            skLineSegment(sketch, "E64.34.3", {"start": v(41.93, -126.59) * mm, "end": v(40.75, -122.96) * mm});
            skLineSegment(sketch, "E64.34.4", {"start": v(40.03, -123.2) * mm, "end": v(40.75, -122.96) * mm});
            skLineSegment(sketch, "E64.34.5", {"start": v(40.03, -123.2) * mm, "end": v(39.3, -123.44) * mm});
            skLineSegment(sketch, "E64.35.0", {"start": v(53.54, -122.13) * mm, "end": v(52, -118.65) * mm});
            skLineSegment(sketch, "E64.35.1", {"start": v(54.24, -121.82) * mm, "end": v(53.54, -122.13) * mm});
            skLineSegment(sketch, "E64.35.2", {"start": v(54.24, -121.82) * mm, "end": v(54.93, -121.51) * mm});
            skLineSegment(sketch, "E64.35.3", {"start": v(54.93, -121.51) * mm, "end": v(53.38, -118.03) * mm});
            skLineSegment(sketch, "E64.35.4", {"start": v(52.69, -118.34) * mm, "end": v(53.38, -118.03) * mm});
            skLineSegment(sketch, "E64.35.5", {"start": v(52.69, -118.34) * mm, "end": v(52, -118.65) * mm});
            skLineSegment(sketch, "E64.37.0", {"start": v(77.76, -108.33) * mm, "end": v(75.53, -105.25) * mm});
            skLineSegment(sketch, "E64.37.1", {"start": v(78.38, -107.88) * mm, "end": v(77.76, -108.33) * mm});
            skLineSegment(sketch, "E64.37.2", {"start": v(78.38, -107.88) * mm, "end": v(79, -107.43) * mm});
            skLineSegment(sketch, "E64.37.3", {"start": v(79, -107.43) * mm, "end": v(76.76, -104.35) * mm});
            skLineSegment(sketch, "E64.37.4", {"start": v(76.14, -104.8) * mm, "end": v(76.76, -104.35) * mm});
            skLineSegment(sketch, "E64.37.5", {"start": v(76.14, -104.8) * mm, "end": v(75.53, -105.25) * mm});
            skLineSegment(sketch, "E64.38.0", {"start": v(88.66, -99.6) * mm, "end": v(86.11, -96.78) * mm});
            skLineSegment(sketch, "E64.38.1", {"start": v(89.23, -99.1) * mm, "end": v(88.66, -99.6) * mm});
            skLineSegment(sketch, "E64.38.2", {"start": v(89.23, -99.1) * mm, "end": v(89.8, -98.59) * mm});
            skLineSegment(sketch, "E64.38.3", {"start": v(89.8, -98.59) * mm, "end": v(87.25, -95.76) * mm});
            skLineSegment(sketch, "E64.38.4", {"start": v(86.68, -96.27) * mm, "end": v(87.25, -95.76) * mm});
            skLineSegment(sketch, "E64.38.5", {"start": v(86.68, -96.27) * mm, "end": v(86.11, -96.78) * mm});
            skLineSegment(sketch, "E64.39.0", {"start": v(98.59, -89.8) * mm, "end": v(95.76, -87.25) * mm});
            skLineSegment(sketch, "E64.39.1", {"start": v(99.1, -89.23) * mm, "end": v(98.59, -89.8) * mm});
            skLineSegment(sketch, "E64.39.2", {"start": v(99.1, -89.23) * mm, "end": v(99.6, -88.66) * mm});
            skLineSegment(sketch, "E64.39.3", {"start": v(99.6, -88.66) * mm, "end": v(96.78, -86.11) * mm});
            skLineSegment(sketch, "E64.39.4", {"start": v(96.27, -86.68) * mm, "end": v(96.78, -86.11) * mm});
            skLineSegment(sketch, "E64.39.5", {"start": v(96.27, -86.68) * mm, "end": v(95.76, -87.25) * mm});
            skLineSegment(sketch, "E64.40.0", {"start": v(107.43, -79) * mm, "end": v(104.35, -76.76) * mm});
            skLineSegment(sketch, "E64.40.1", {"start": v(107.88, -78.38) * mm, "end": v(107.43, -79) * mm});
            skLineSegment(sketch, "E64.40.2", {"start": v(107.88, -78.38) * mm, "end": v(108.33, -77.76) * mm});
            skLineSegment(sketch, "E64.40.3", {"start": v(108.33, -77.76) * mm, "end": v(105.25, -75.53) * mm});
            skLineSegment(sketch, "E64.40.4", {"start": v(104.8, -76.14) * mm, "end": v(105.25, -75.53) * mm});
            skLineSegment(sketch, "E64.40.5", {"start": v(104.8, -76.14) * mm, "end": v(104.35, -76.76) * mm});
            skLineSegment(sketch, "E64.42.0", {"start": v(121.51, -54.93) * mm, "end": v(118.03, -53.38) * mm});
            skLineSegment(sketch, "E64.42.1", {"start": v(121.82, -54.24) * mm, "end": v(121.51, -54.93) * mm});
            skLineSegment(sketch, "E64.42.2", {"start": v(121.82, -54.24) * mm, "end": v(122.13, -53.54) * mm});
            skLineSegment(sketch, "E64.42.3", {"start": v(122.13, -53.54) * mm, "end": v(118.65, -52) * mm});
            skLineSegment(sketch, "E64.42.4", {"start": v(118.34, -52.69) * mm, "end": v(118.65, -52) * mm});
            skLineSegment(sketch, "E64.42.5", {"start": v(118.34, -52.69) * mm, "end": v(118.03, -53.38) * mm});
            skLineSegment(sketch, "E64.43.0", {"start": v(126.59, -41.93) * mm, "end": v(122.96, -40.75) * mm});
            skLineSegment(sketch, "E64.43.1", {"start": v(126.82, -41.2) * mm, "end": v(126.59, -41.93) * mm});
            skLineSegment(sketch, "E64.43.2", {"start": v(126.82, -41.2) * mm, "end": v(127.06, -40.48) * mm});
            skLineSegment(sketch, "E64.43.3", {"start": v(127.06, -40.48) * mm, "end": v(123.44, -39.3) * mm});
            skLineSegment(sketch, "E64.43.4", {"start": v(123.2, -40.03) * mm, "end": v(123.44, -39.3) * mm});
            skLineSegment(sketch, "E64.43.5", {"start": v(123.2, -40.03) * mm, "end": v(122.96, -40.75) * mm});
            skLineSegment(sketch, "E64.44.0", {"start": v(130.28, -28.47) * mm, "end": v(126.55, -27.68) * mm});
            skLineSegment(sketch, "E64.44.1", {"start": v(130.44, -27.73) * mm, "end": v(130.28, -28.47) * mm});
            skLineSegment(sketch, "E64.44.2", {"start": v(130.44, -27.73) * mm, "end": v(130.6, -26.98) * mm});
            skLineSegment(sketch, "E64.44.3", {"start": v(130.6, -26.98) * mm, "end": v(126.87, -26.19) * mm});
            skLineSegment(sketch, "E64.44.4", {"start": v(126.7, -26.93) * mm, "end": v(126.87, -26.19) * mm});
            skLineSegment(sketch, "E64.44.5", {"start": v(126.7, -26.93) * mm, "end": v(126.55, -27.68) * mm});
            skLineSegment(sketch, "E64.45.0", {"start": v(132.54, -14.7) * mm, "end": v(128.75, -14.3) * mm});
            skLineSegment(sketch, "E64.45.1", {"start": v(132.62, -13.94) * mm, "end": v(132.54, -14.7) * mm});
            skLineSegment(sketch, "E64.45.2", {"start": v(132.62, -13.94) * mm, "end": v(132.7, -13.18) * mm});
            skLineSegment(sketch, "E64.45.3", {"start": v(132.7, -13.18) * mm, "end": v(128.91, -12.78) * mm});
            skLineSegment(sketch, "E64.45.4", {"start": v(128.83, -13.54) * mm, "end": v(128.91, -12.78) * mm});
            skLineSegment(sketch, "E64.45.5", {"start": v(128.83, -13.54) * mm, "end": v(128.75, -14.3) * mm});
            skLineSegment(sketch, "E64.47.0", {"start": v(132.7, 13.18) * mm, "end": v(128.91, 12.78) * mm});
            skLineSegment(sketch, "E64.47.1", {"start": v(132.62, 13.94) * mm, "end": v(132.7, 13.18) * mm});
            skLineSegment(sketch, "E64.47.2", {"start": v(132.62, 13.94) * mm, "end": v(132.54, 14.7) * mm});
            skLineSegment(sketch, "E64.47.3", {"start": v(132.54, 14.7) * mm, "end": v(128.75, 14.3) * mm});
            skLineSegment(sketch, "E64.47.4", {"start": v(128.83, 13.54) * mm, "end": v(128.75, 14.3) * mm});
            skLineSegment(sketch, "E64.47.5", {"start": v(128.83, 13.54) * mm, "end": v(128.91, 12.78) * mm});
            skLineSegment(sketch, "E64.48.0", {"start": v(130.6, 26.98) * mm, "end": v(126.87, 26.19) * mm});
            skLineSegment(sketch, "E64.48.1", {"start": v(130.44, 27.73) * mm, "end": v(130.6, 26.98) * mm});
            skLineSegment(sketch, "E64.48.2", {"start": v(130.44, 27.73) * mm, "end": v(130.28, 28.47) * mm});
            skLineSegment(sketch, "E64.48.3", {"start": v(130.28, 28.47) * mm, "end": v(126.55, 27.68) * mm});
            skLineSegment(sketch, "E64.48.4", {"start": v(126.7, 26.93) * mm, "end": v(126.55, 27.68) * mm});
            skLineSegment(sketch, "E64.48.5", {"start": v(126.7, 26.93) * mm, "end": v(126.87, 26.19) * mm});
            skLineSegment(sketch, "E64.49.0", {"start": v(127.06, 40.48) * mm, "end": v(123.44, 39.3) * mm});
            skLineSegment(sketch, "E64.49.1", {"start": v(126.82, 41.2) * mm, "end": v(127.06, 40.48) * mm});
            skLineSegment(sketch, "E64.49.2", {"start": v(126.82, 41.2) * mm, "end": v(126.59, 41.93) * mm});
            skLineSegment(sketch, "E64.49.3", {"start": v(126.59, 41.93) * mm, "end": v(122.96, 40.75) * mm});
            skLineSegment(sketch, "E64.49.4", {"start": v(123.2, 40.03) * mm, "end": v(122.96, 40.75) * mm});
            skLineSegment(sketch, "E64.49.5", {"start": v(123.2, 40.03) * mm, "end": v(123.44, 39.3) * mm});
            skLineSegment(sketch, "E64.50.0", {"start": v(122.13, 53.54) * mm, "end": v(118.65, 52) * mm});
            skLineSegment(sketch, "E64.50.1", {"start": v(121.82, 54.24) * mm, "end": v(122.13, 53.54) * mm});
            skLineSegment(sketch, "E64.50.2", {"start": v(121.82, 54.24) * mm, "end": v(121.51, 54.93) * mm});
            skLineSegment(sketch, "E64.50.3", {"start": v(121.51, 54.93) * mm, "end": v(118.03, 53.38) * mm});
            skLineSegment(sketch, "E64.50.4", {"start": v(118.34, 52.69) * mm, "end": v(118.03, 53.38) * mm});
            skLineSegment(sketch, "E64.50.5", {"start": v(118.34, 52.69) * mm, "end": v(118.65, 52) * mm});
            skLineSegment(sketch, "E64.52.0", {"start": v(108.33, 77.76) * mm, "end": v(105.25, 75.53) * mm});
            skLineSegment(sketch, "E64.52.1", {"start": v(107.88, 78.38) * mm, "end": v(108.33, 77.76) * mm});
            skLineSegment(sketch, "E64.52.2", {"start": v(107.88, 78.38) * mm, "end": v(107.43, 79) * mm});
            skLineSegment(sketch, "E64.52.3", {"start": v(107.43, 79) * mm, "end": v(104.35, 76.76) * mm});
            skLineSegment(sketch, "E64.52.4", {"start": v(104.8, 76.14) * mm, "end": v(104.35, 76.76) * mm});
            skLineSegment(sketch, "E64.52.5", {"start": v(104.8, 76.14) * mm, "end": v(105.25, 75.53) * mm});
            skLineSegment(sketch, "E64.53.0", {"start": v(99.6, 88.66) * mm, "end": v(96.78, 86.11) * mm});
            skLineSegment(sketch, "E64.53.1", {"start": v(99.1, 89.23) * mm, "end": v(99.6, 88.66) * mm});
            skLineSegment(sketch, "E64.53.2", {"start": v(99.1, 89.23) * mm, "end": v(98.59, 89.8) * mm});
            skLineSegment(sketch, "E64.53.3", {"start": v(98.59, 89.8) * mm, "end": v(95.76, 87.25) * mm});
            skLineSegment(sketch, "E64.53.4", {"start": v(96.27, 86.68) * mm, "end": v(95.76, 87.25) * mm});
            skLineSegment(sketch, "E64.53.5", {"start": v(96.27, 86.68) * mm, "end": v(96.78, 86.11) * mm});
            skLineSegment(sketch, "E64.54.0", {"start": v(89.8, 98.59) * mm, "end": v(87.25, 95.76) * mm});
            skLineSegment(sketch, "E64.54.1", {"start": v(89.23, 99.1) * mm, "end": v(89.8, 98.59) * mm});
            skLineSegment(sketch, "E64.54.2", {"start": v(89.23, 99.1) * mm, "end": v(88.66, 99.6) * mm});
            skLineSegment(sketch, "E64.54.3", {"start": v(88.66, 99.6) * mm, "end": v(86.11, 96.78) * mm});
            skLineSegment(sketch, "E64.54.4", {"start": v(86.68, 96.27) * mm, "end": v(86.11, 96.78) * mm});
            skLineSegment(sketch, "E64.54.5", {"start": v(86.68, 96.27) * mm, "end": v(87.25, 95.76) * mm});
            skLineSegment(sketch, "E64.55.0", {"start": v(79, 107.43) * mm, "end": v(76.76, 104.35) * mm});
            skLineSegment(sketch, "E64.55.1", {"start": v(78.38, 107.88) * mm, "end": v(79, 107.43) * mm});
            skLineSegment(sketch, "E64.55.2", {"start": v(78.38, 107.88) * mm, "end": v(77.76, 108.33) * mm});
            skLineSegment(sketch, "E64.55.3", {"start": v(77.76, 108.33) * mm, "end": v(75.53, 105.25) * mm});
            skLineSegment(sketch, "E64.55.4", {"start": v(76.14, 104.8) * mm, "end": v(75.53, 105.25) * mm});
            skLineSegment(sketch, "E64.55.5", {"start": v(76.14, 104.8) * mm, "end": v(76.76, 104.35) * mm});
            skLineSegment(sketch, "E64.57.0", {"start": v(54.93, 121.51) * mm, "end": v(53.38, 118.03) * mm});
            skLineSegment(sketch, "E64.57.1", {"start": v(54.24, 121.82) * mm, "end": v(54.93, 121.51) * mm});
            skLineSegment(sketch, "E64.57.2", {"start": v(54.24, 121.82) * mm, "end": v(53.54, 122.13) * mm});
            skLineSegment(sketch, "E64.57.3", {"start": v(53.54, 122.13) * mm, "end": v(52, 118.65) * mm});
            skLineSegment(sketch, "E64.57.4", {"start": v(52.69, 118.34) * mm, "end": v(52, 118.65) * mm});
            skLineSegment(sketch, "E64.57.5", {"start": v(52.69, 118.34) * mm, "end": v(53.38, 118.03) * mm});
            skPoint(sketch, "E64.center", {"position": v(0, 0) * mm});
            skLineSegment(sketch, "E65.2.58.0", {"start": v(41.93, 126.59) * mm, "end": v(40.75, 122.96) * mm});
            skLineSegment(sketch, "E65.3.58.0", {"start": v(41.2, 126.82) * mm, "end": v(41.93, 126.59) * mm});
            skLineSegment(sketch, "E65.6.58.0", {"start": v(41.2, 126.82) * mm, "end": v(40.48, 127.06) * mm});
            skLineSegment(sketch, "E65.9.58.0", {"start": v(40.48, 127.06) * mm, "end": v(39.3, 123.44) * mm});
            skLineSegment(sketch, "E65.12.58.0", {"start": v(40.03, 123.2) * mm, "end": v(39.3, 123.44) * mm});
            skLineSegment(sketch, "E65.15.58.0", {"start": v(40.03, 123.2) * mm, "end": v(40.75, 122.96) * mm});
            skLineSegment(sketch, "E65.2.59.0", {"start": v(28.47, 130.28) * mm, "end": v(27.68, 126.55) * mm});
            skLineSegment(sketch, "E65.3.59.0", {"start": v(27.73, 130.44) * mm, "end": v(28.47, 130.28) * mm});
            skLineSegment(sketch, "E65.6.59.0", {"start": v(27.73, 130.44) * mm, "end": v(26.98, 130.6) * mm});
            skLineSegment(sketch, "E65.9.59.0", {"start": v(26.98, 130.6) * mm, "end": v(26.19, 126.87) * mm});
            skLineSegment(sketch, "E65.12.59.0", {"start": v(26.93, 126.7) * mm, "end": v(26.19, 126.87) * mm});
            skLineSegment(sketch, "E65.15.59.0", {"start": v(26.93, 126.7) * mm, "end": v(27.68, 126.55) * mm});
            skSolve(sketch);
        }
        {
            var Q0;
            Q0=qSketchRegion(id+"F26",true);
            extrude(context, id + "F27", {"entities" : qUnion([Q0]), "operationType" : NewBodyOperationType.ADD, "depth" : 2.54 * mm});
        }
    });
